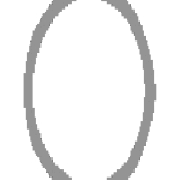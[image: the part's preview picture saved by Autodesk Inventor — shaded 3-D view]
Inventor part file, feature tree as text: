
AUTODESK INVENTOR PART (.ipt)
format: ipt  version: 2021 (Build 250183000, 183)  size: 113,664 bytes
history: native  units: in
note: dims shown in document units (in); Inventor stores cm internally (conversion verified against a paired STEP export)
features: other x4, sketch x3, plane x1
ambient origin geometry x8: Origin, YZ Plane, XZ Plane, XY Plane, X Axis, Y Axis, Z Axis, Center Point
bodies: Solid1 (feature_tree), Body (feature_tree)
feature tree (8):
  other  "Driven Length"
  other  "Frame Generator"
  other  "Start Plane"
  other  "End Plane"
  sketch  "Sketch"  dims[d2=8.0in d4=-0.0in d5=8.0in d6=0.12in d7=0.0in d8=90.0deg d9=8.0in]
  sketch  "Sketch2"  dims[d0=1.0in]
  plane  "Work Plane3"
  sketch  "Sketch3"  dims[d1=0.065in]
